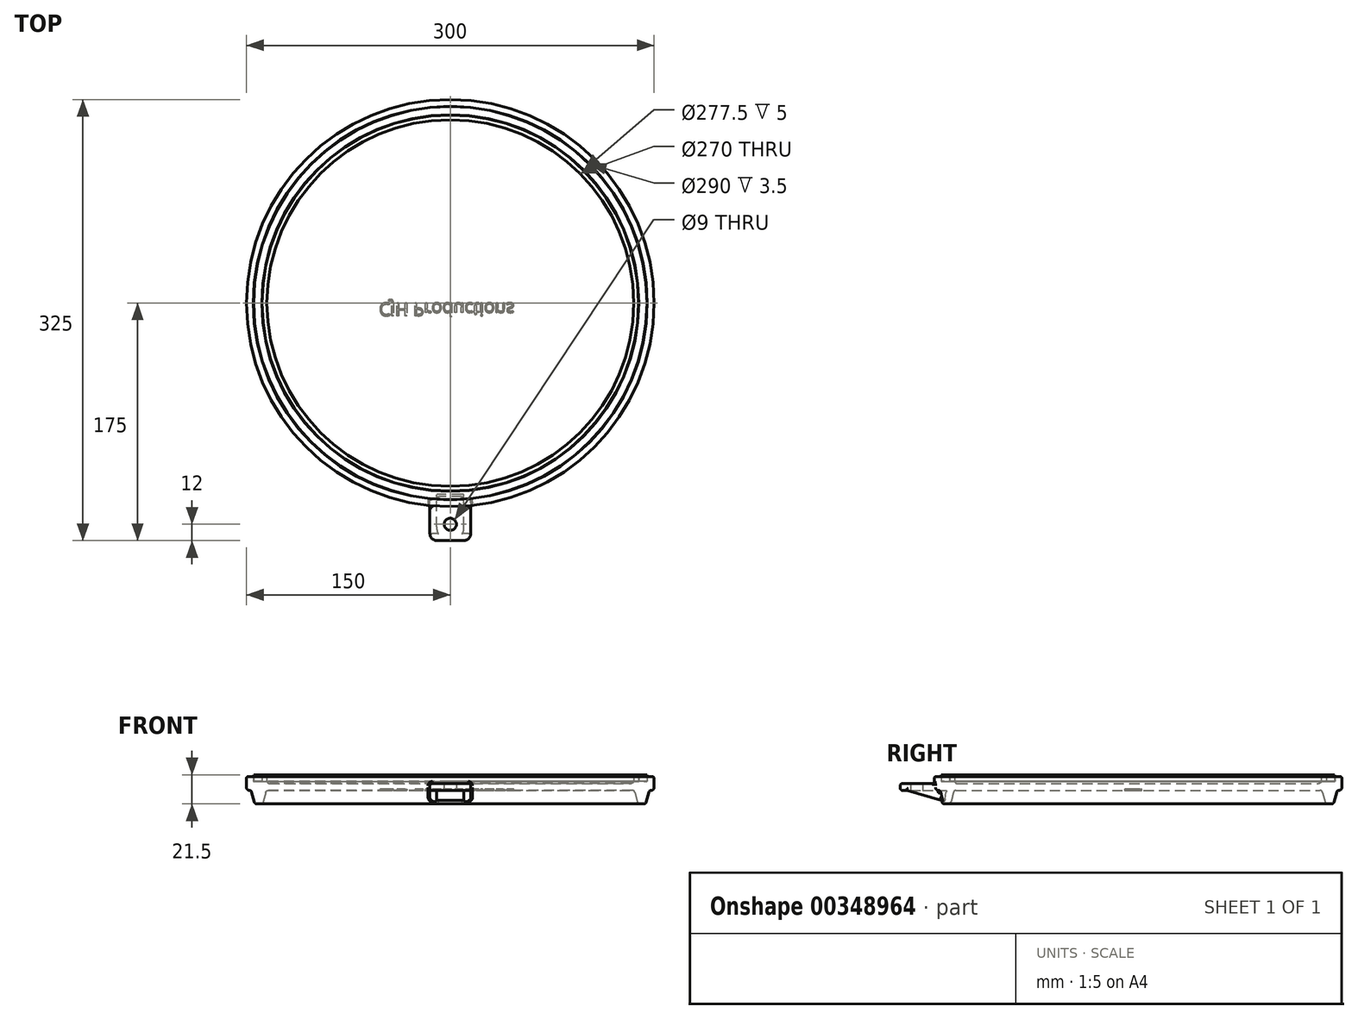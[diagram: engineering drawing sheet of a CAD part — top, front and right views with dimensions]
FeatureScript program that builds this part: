
annotation { "Feature Type Name" : "Feature", "Feature Type Description" : "" }
export const myFeature = defineFeature(function(context is Context, id is Id, definition is map)
    precondition{}
    {
        {
            var Q0;
            Q0=qCreatedBy(makeId("Front.planeOp"),FACE);
            var sketch = newSketch(context, id + "F0", { "sketchPlane" : qUnion([Q0])});
            skLineSegment(sketch, "E0", {"start": v(0, 0) * mm, "end": v(-133.94, 0) * mm});
            skLineSegment(sketch, "E1", {"start": v(-150, 2) * mm, "end": v(-150, 9) * mm});
            skLineSegment(sketch, "E2", {"start": v(-149, 10) * mm, "end": v(-145, 10) * mm});
            skLineSegment(sketch, "E3", {"start": v(-145, 10) * mm, "end": v(-145, 6.5) * mm});
            skLineSegment(sketch, "E4", {"start": v(-145, 6.5) * mm, "end": v(-138.5, 6.5) * mm});
            skLineSegment(sketch, "E5", {"start": v(-138.5, 6.5) * mm, "end": v(-138.5, 10) * mm});
            skLineSegment(sketch, "E6", {"start": v(-138.5, 10) * mm, "end": v(-136, 10) * mm});
            skLineSegment(sketch, "E7", {"start": v(-135, 9) * mm, "end": v(-135, 7) * mm});
            skLineSegment(sketch, "E8", {"start": v(-133, 5) * mm, "end": v(0, 5) * mm});
            skLineSegment(sketch, "E9", {"start": v(0, -14.03) * mm, "end": v(0, 19) * mm, "construction": true});
            skLineSegment(sketch, "E10", {"start": v(-146.12, -1.51) * mm, "end": v(-144.38, -8.49) * mm});
            skLineSegment(sketch, "E11", {"start": v(-142.44, -10) * mm, "end": v(-139.56, -10) * mm});
            skLineSegment(sketch, "E12", {"start": v(-137.62, -8.49) * mm, "end": v(-135.88, -1.51) * mm});
            skPoint(sketch, "E13.visualSharp", {"position": v(-150, 0) * mm});
            skArc(sketch, "E13.filletArc", {"start": v(-150, 2) * mm, "mid": v(-149.43, 0.6) * mm, "end": v(-148.03, 0) * mm});
            skArc(sketch, "E14.filletArc", {"start": v(-133.94, 0) * mm, "mid": v(-135.17, -0.42) * mm, "end": v(-135.88, -1.51) * mm});
            skPoint(sketch, "E15.newPointB", {"position": v(-146.5, 0) * mm});
            skArc(sketch, "E15.filletArc", {"start": v(-146.12, -1.51) * mm, "mid": v(-146.82, -0.43) * mm, "end": v(-148.03, 0) * mm});
            skPoint(sketch, "E16.visualSharp", {"position": v(-144, -10) * mm});
            skArc(sketch, "E16.filletArc", {"start": v(-144.38, -8.49) * mm, "mid": v(-143.67, -9.58) * mm, "end": v(-142.44, -10) * mm});
            skPoint(sketch, "E17.visualSharp", {"position": v(-138, -10) * mm});
            skArc(sketch, "E17.filletArc", {"start": v(-139.56, -10) * mm, "mid": v(-138.33, -9.58) * mm, "end": v(-137.62, -8.49) * mm});
            skPoint(sketch, "E18.visualSharp", {"position": v(-135, 5) * mm});
            skArc(sketch, "E18.filletArc", {"start": v(-135, 7) * mm, "mid": v(-134.41, 5.59) * mm, "end": v(-133, 5) * mm});
            skPoint(sketch, "E19.visualSharp", {"position": v(-150, 10) * mm});
            skArc(sketch, "E19.filletArc", {"start": v(-149, 10) * mm, "mid": v(-149.7, 9.7) * mm, "end": v(-150, 9) * mm});
            skPoint(sketch, "E20.visualSharp", {"position": v(-135, 10) * mm});
            skArc(sketch, "E20.filletArc", {"start": v(-135, 9) * mm, "mid": v(-135.3, 9.7) * mm, "end": v(-136, 10) * mm});
            skLineSegment(sketch, "E21", {"start": v(0, 0) * mm, "end": v(0, 5) * mm});
            skSolve(sketch);
        }
        {
            var Q0;
            Q0=makeQuery(id+"F0.imprint","IMPRINT",FACE,{"disambiguationData":[TD([[makeQuery(id+"F0.imprint","IMPRINT",EDGE,{"derivedFrom":sQuery(id+"F0.wireOp",EDGE,"E0")}),-1.0]])]});
            var Q1;
            Q1=sQuery(id+"F0.wireOp",EDGE,"E9");
            revolve(context, id + "F1", {"entities" : qUnion([Q0]), "axis" : qUnion([Q1]), "revolveType" : RevolveType.FULL});
        }
        {
            var Q0;
            Q0=qCreatedBy(makeId("Front.planeOp"),FACE);
            var sketch = newSketch(context, id + "F2", { "sketchPlane" : qUnion([Q0])});
            skLineSegment(sketch, "E22", {"start": v(-144, 5) * mm, "end": v(-175, 5) * mm});
            skLineSegment(sketch, "E23", {"start": v(-175, 5) * mm, "end": v(-175, 0) * mm});
            skLineSegment(sketch, "E24", {"start": v(-175, 0) * mm, "end": v(-141, 0) * mm});
            skLineSegment(sketch, "E25", {"start": v(-170, 0) * mm, "end": v(-142.44, -8) * mm});
            skLineSegment(sketch, "E26", {"start": v(-144, 5) * mm, "end": v(-141, 0) * mm});
            skLineSegment(sketch, "E27", {"start": v(-142.44, -8) * mm, "end": v(-141, 0) * mm});
            skSolve(sketch);
        }
        {
            var Q0;
            Q0=makeQuery(id+"F2.imprint","IMPRINT",FACE,{"disambiguationData":[TD([[makeQuery(id+"F2.imprint","IMPRINT",EDGE,{"derivedFrom":sQuery(id+"F2.wireOp",EDGE,"E22")}),1.0]])]});
            var Q1;
            {var subQ2=sQuery(id+"F2.wireOp",EDGE,"E25");Q1=makeQuery(id+"F2.imprint","IMPRINT",FACE,{"disambiguationData":[TD([[makeQuery(id+"F2.imprint","IMPRINT",EDGE,{"derivedFrom":subQ2}),1.0]])]});}
            extrude(context, id + "F3", {"entities" : qUnion([Q0, Q1]), "depth" : 30 * mm, "symmetric" : true});
        }
        {
            var Q0;
            {var subQ2=sQuery(id+"F2.wireOp",EDGE,"E25");Q0=makeQuery(id+"F2.imprint","IMPRINT",FACE,{"disambiguationData":[TD([[makeQuery(id+"F2.imprint","IMPRINT",EDGE,{"derivedFrom":subQ2}),1.0]])]});}
            var Q1;
            {var subQ0=sQuery(id+"F2.wireOp",EDGE,"E22");var subQ1=sQuery(id+"F2.wireOp",EDGE,"E23");var subQ2=sQuery(id+"F2.wireOp",EDGE,"E24");Q1=makeQuery(id+"F3.boolean.opBoolean","SPLIT",FACE,{"disambiguationData":[TD([makeQuery(id+"F1.opRevolve","SWEPT_FACE",FACE,{"disambiguationData":[OSD([sQuery(id+"F0.wireOp",EDGE,"E1")])]})])],"derivedFrom":makeQuery(id+"F3.opExtrude","CAP_FACE",FACE,{"disambiguationData":[OSD([subQ0,subQ1,subQ2,sQuery(id+"F2.wireOp",EDGE,"E26")])],"isStart":false})});}
            var Q2;
            {var subQ0=sQuery(id+"F2.wireOp",EDGE,"E22");var subQ1=sQuery(id+"F2.wireOp",EDGE,"E23");var subQ2=sQuery(id+"F2.wireOp",EDGE,"E24");Q2=makeQuery(id+"F3.boolean.opBoolean","SPLIT",FACE,{"disambiguationData":[TD([makeQuery(id+"F1.opRevolve","SWEPT_FACE",FACE,{"disambiguationData":[OSD([sQuery(id+"F0.wireOp",EDGE,"E1")])]})])],"derivedFrom":makeQuery(id+"F3.opExtrude","CAP_FACE",FACE,{"disambiguationData":[OSD([subQ0,subQ1,subQ2,sQuery(id+"F2.wireOp",EDGE,"E26")])],"isStart":true})});}
            extrude(context, id + "F4", {"entities" : qUnion([Q0]), "operationType" : NewBodyOperationType.REMOVE, "endBoundEntityFace" : qUnion([Q1]), "depth" : 20 * mm, "hasSecondDirection" : true, "secondDirectionBound" : BoundingType.UP_TO_SURFACE, "secondDirectionOppositeDirection" : true, "secondDirectionBoundEntityFace" : qUnion([Q2]), "secondDirectionDepth" : 25 * mm, "symmetric" : true});
        }
        {
            var Q0;
            Q0=makeQuery(id+"F1.opRevolve","SWEPT_BODY",BODY,{"disambiguationData":[OSD([sQuery(id+"F0.wireOp",EDGE,"E0"),sQuery(id+"F0.wireOp",EDGE,"E1"),sQuery(id+"F0.wireOp",EDGE,"E2"),sQuery(id+"F0.wireOp",EDGE,"E3"),sQuery(id+"F0.wireOp",EDGE,"E4"),sQuery(id+"F0.wireOp",EDGE,"E5"),sQuery(id+"F0.wireOp",EDGE,"E6"),sQuery(id+"F0.wireOp",EDGE,"E7"),sQuery(id+"F0.wireOp",EDGE,"E8"),sQuery(id+"F0.wireOp",EDGE,"E10"),sQuery(id+"F0.wireOp",EDGE,"E11"),sQuery(id+"F0.wireOp",EDGE,"E12"),sQuery(id+"F0.wireOp",EDGE,"E13.filletArc"),sQuery(id+"F0.wireOp",EDGE,"E14.filletArc"),sQuery(id+"F0.wireOp",EDGE,"E15.filletArc"),sQuery(id+"F0.wireOp",EDGE,"E16.filletArc"),sQuery(id+"F0.wireOp",EDGE,"E17.filletArc"),sQuery(id+"F0.wireOp",EDGE,"E18.filletArc"),sQuery(id+"F0.wireOp",EDGE,"E19.filletArc"),sQuery(id+"F0.wireOp",EDGE,"E20.filletArc"),sQuery(id+"F0.wireOp",EDGE,"E21")])]});
            var Q1;
            Q1=makeQuery(id+"F3.opExtrude","SWEPT_BODY",BODY,{"disambiguationData":[OSD([sQuery(id+"F2.wireOp",EDGE,"E22"),sQuery(id+"F2.wireOp",EDGE,"E23"),sQuery(id+"F2.wireOp",EDGE,"E24"),sQuery(id+"F2.wireOp",EDGE,"E25"),sQuery(id+"F2.wireOp",EDGE,"E26"),sQuery(id+"F2.wireOp",EDGE,"E27")])]});
            booleanBodies(context, id + "F5", {"operationType" : BooleanOperationType.UNION, "tools" : qUnion([Q0, Q1])});
        }
        {
            var Q0;
            {var subQ0=sQuery(id+"F2.wireOp",EDGE,"E23");var subQ4=sQuery(id+"F2.wireOp",EDGE,"E24");Q0=makeQuery(id+"F5.opBoolean","SPLIT",FACE,{"disambiguationData":[TD([makeQuery(id+"F3.opExtrude","SWEPT_FACE",FACE,{"disambiguationData":[OSD([subQ0])]})])],"derivedFrom":makeQuery(id+"F4.boolean.opBoolean","MERGE",FACE,{"derivedFrom":[makeQuery(id+"F3.opExtrude","SWEPT_FACE",FACE,{"disambiguationData":[OSD([subQ4])]}),makeQuery(id+"F4.opExtrude","SWEPT_FACE",FACE,{"disambiguationData":[OSD([subQ4])]})]})});}
            var sketch = newSketch(context, id + "F6", { "sketchPlane" : qUnion([Q0])});
            skCircle(sketch, "E28", {"center": v(-163, 0) * mm, "radius": 4.5 * mm});
            skSolve(sketch);
        }
        {
            var Q0;
            Q0=makeQuery(id+"F6.imprint","IMPRINT",FACE,{"disambiguationData":[TD([[makeQuery(id+"F6.imprint","IMPRINT",EDGE,{"derivedFrom":sQuery(id+"F6.wireOp",EDGE,"E28")}),1.0]])]});
            extrude(context, id + "F7", {"entities" : qUnion([Q0]), "operationType" : NewBodyOperationType.REMOVE, "endBound" : BoundingType.THROUGH_ALL, "oppositeDirection" : true, "depth" : 25 * mm});
        }
        {
            var Q0;
            Q0=makeQuery(id+"F3.opExtrude","CAP_EDGE",EDGE,{"disambiguationData":[OSD([sQuery(id+"F2.wireOp",EDGE,"E23")])],"isStart":false});
            var Q1;
            Q1=makeQuery(id+"F3.opExtrude","CAP_EDGE",EDGE,{"disambiguationData":[OSD([sQuery(id+"F2.wireOp",EDGE,"E23")])],"isStart":true});
            fillet(context, id + "F8", {"entities" : qUnion([Q0, Q1]), "radius" : 5 * mm, "tangentPropagation" : true, "allowEdgeOverflow" : false});
        }
        {
            var Q0;
            Q0=makeQuery(id+"F3.opExtrude","SWEPT_EDGE",EDGE,{"disambiguationData":[OSD([sQuery(id+"F2.wireOp",EDGE,"E23"),sQuery(id+"F2.wireOp",EDGE,"E24")])]});
            var Q1;
            {var subQ0=sQuery(id+"F2.wireOp",EDGE,"E23");var subQ4=sQuery(id+"F2.wireOp",EDGE,"E24");Q1=makeQuery(id+"F8.opFillet","BLEND_EDGE",EDGE,{"blendedFrom":[makeQuery(id+"F3.opExtrude","CAP_EDGE",EDGE,{"disambiguationData":[OSD([subQ0])],"isStart":true}),makeQuery(id+"F5.opBoolean","SPLIT",FACE,{"disambiguationData":[TD([makeQuery(id+"F3.opExtrude","SWEPT_FACE",FACE,{"disambiguationData":[OSD([subQ0])]})])],"derivedFrom":makeQuery(id+"F4.boolean.opBoolean","MERGE",FACE,{"derivedFrom":[makeQuery(id+"F3.opExtrude","SWEPT_FACE",FACE,{"disambiguationData":[OSD([subQ4])]}),makeQuery(id+"F4.opExtrude","SWEPT_FACE",FACE,{"disambiguationData":[OSD([subQ4])]})]})})],"blendedInto":[makeQuery(id+"F5.opBoolean","SPLIT",FACE,{"disambiguationData":[TD([makeQuery(id+"F3.opExtrude","SWEPT_FACE",FACE,{"disambiguationData":[OSD([subQ0])]})])],"derivedFrom":makeQuery(id+"F4.boolean.opBoolean","MERGE",FACE,{"derivedFrom":[makeQuery(id+"F3.opExtrude","SWEPT_FACE",FACE,{"disambiguationData":[OSD([subQ4])]}),makeQuery(id+"F4.opExtrude","SWEPT_FACE",FACE,{"disambiguationData":[OSD([subQ4])]})]})})]});}
            var Q2;
            Q2=makeQuery(id+"F3.opExtrude","CAP_EDGE",EDGE,{"disambiguationData":[OSD([sQuery(id+"F2.wireOp",EDGE,"E25")])],"isStart":true});
            var Q3;
            Q3=makeQuery(id+"F3.opExtrude","CAP_EDGE",EDGE,{"disambiguationData":[OSD([sQuery(id+"F2.wireOp",EDGE,"E25")])],"isStart":false});
            var Q4;
            Q4=makeQuery(id+"F4.boolean.opBoolean","COPY",EDGE,{"derivedFrom":makeQuery(id+"F4.opExtrude","CAP_EDGE",EDGE,{"disambiguationData":[OSD([sQuery(id+"F2.wireOp",EDGE,"E25")])],"isStart":true})});
            var Q5;
            Q5=makeQuery(id+"F4.boolean.opBoolean","COPY",EDGE,{"derivedFrom":makeQuery(id+"F4.opExtrude","CAP_EDGE",EDGE,{"disambiguationData":[OSD([sQuery(id+"F2.wireOp",EDGE,"E25")])],"isStart":false})});
            var Q6;
            Q6=makeQuery(id+"F3.opExtrude","SWEPT_EDGE",EDGE,{"disambiguationData":[OSD([sQuery(id+"F2.wireOp",EDGE,"E22"),sQuery(id+"F2.wireOp",EDGE,"E23")])]});
            var Q7;
            {var subQ0=sQuery(id+"F2.wireOp",EDGE,"E24");var subQ1=sQuery(id+"F2.wireOp",EDGE,"E25");Q7=makeQuery(id+"F5.opBoolean","SPLIT",EDGE,{"disambiguationData":[TD([makeQuery(id+"F3.opExtrude","SWEPT_FACE",FACE,{"disambiguationData":[OSD([subQ1])]})])],"derivedFrom":makeQuery(id+"F4.boolean.opBoolean","COPY",EDGE,{"derivedFrom":makeQuery(id+"F4.opExtrude","CAP_EDGE",EDGE,{"disambiguationData":[OSD([subQ0])],"isStart":false})})});}
            var Q8;
            {var subQ0=sQuery(id+"F2.wireOp",EDGE,"E24");var subQ1=sQuery(id+"F2.wireOp",EDGE,"E25");Q8=makeQuery(id+"F5.opBoolean","SPLIT",EDGE,{"disambiguationData":[TD([makeQuery(id+"F3.opExtrude","SWEPT_FACE",FACE,{"disambiguationData":[OSD([subQ1])]})])],"derivedFrom":makeQuery(id+"F4.boolean.opBoolean","COPY",EDGE,{"derivedFrom":makeQuery(id+"F4.opExtrude","CAP_EDGE",EDGE,{"disambiguationData":[OSD([subQ0])],"isStart":true})})});}
            fillet(context, id + "F9", {"entities" : qUnion([Q0, Q1, Q2, Q3, Q4, Q5, Q6, Q7, Q8]), "radius" : 1.5 * mm, "tangentPropagation" : true, "allowEdgeOverflow" : false});
        }
        {
            var Q0;
            Q0=makeQuery(id+"F5.opBoolean","INTERSECT",EDGE,{"derivedFrom":[makeQuery(id+"F1.opRevolve","SWEPT_FACE",FACE,{"disambiguationData":[OSD([sQuery(id+"F0.wireOp",EDGE,"E1")])]}),makeQuery(id+"F3.opExtrude","SWEPT_FACE",FACE,{"disambiguationData":[OSD([sQuery(id+"F2.wireOp",EDGE,"E22")])]})]});
            fillet(context, id + "F10", {"entities" : qUnion([Q0]), "radius" : 1.5 * mm, "tangentPropagation" : true, "allowEdgeOverflow" : false});
        }
        {
            var Q0;
            Q0=makeQuery(id+"F1.opRevolve","SWEPT_BODY",BODY,{"disambiguationData":[OSD([sQuery(id+"F0.wireOp",EDGE,"E0"),sQuery(id+"F0.wireOp",EDGE,"E1"),sQuery(id+"F0.wireOp",EDGE,"E2"),sQuery(id+"F0.wireOp",EDGE,"E3"),sQuery(id+"F0.wireOp",EDGE,"E4"),sQuery(id+"F0.wireOp",EDGE,"E5"),sQuery(id+"F0.wireOp",EDGE,"E6"),sQuery(id+"F0.wireOp",EDGE,"E7"),sQuery(id+"F0.wireOp",EDGE,"E8"),sQuery(id+"F0.wireOp",EDGE,"E10"),sQuery(id+"F0.wireOp",EDGE,"E11"),sQuery(id+"F0.wireOp",EDGE,"E12"),sQuery(id+"F0.wireOp",EDGE,"E13.filletArc"),sQuery(id+"F0.wireOp",EDGE,"E14.filletArc"),sQuery(id+"F0.wireOp",EDGE,"E15.filletArc"),sQuery(id+"F0.wireOp",EDGE,"E16.filletArc"),sQuery(id+"F0.wireOp",EDGE,"E17.filletArc"),sQuery(id+"F0.wireOp",EDGE,"E18.filletArc"),sQuery(id+"F0.wireOp",EDGE,"E19.filletArc"),sQuery(id+"F0.wireOp",EDGE,"E20.filletArc"),sQuery(id+"F0.wireOp",EDGE,"E21")])]});
            var Q1;
            Q1=sQuery(id+"F0.wireOp",EDGE,"E9");
            transform(context, id + "F11", {"entities" : qUnion([Q0]), "transformType" : TransformType.ROTATION, "transformAxis" : qUnion([Q1]), "angle" : 90 * degree, "makeCopy" : false});
        }
        {
            var Q0;
            Q0=makeQuery(id+"F1.opRevolve","SWEPT_FACE",FACE,{"disambiguationData":[OSD([sQuery(id+"F0.wireOp",EDGE,"E0")])]});
            var sketch = newSketch(context, id + "F12", { "sketchPlane" : qUnion([Q0])});
            skText(sketch, "E29", { "text": "CJH Productions", "fontName": "OpenSans-Regular.ttf"});
            const initialGuessF12  = {"E29": [-0.0525, -0.00014, 1, 0, 0.00956]};
            skSetInitialGuess(sketch, initialGuessF12);
            skSolve(sketch);
        }
        {
            var Q0;
            Q0 = qSketchRegion(id + "F12", true);
            extrude(context, id + "F13", {"entities" : qUnion([Q0]), "operationType" : NewBodyOperationType.REMOVE, "oppositeDirection" : true, "depth" : 1 * mm, "hasDraft" : true, "draftAngle" : 3 * degree});
        }
        {
            var Q0;
            Q0=qCreatedBy(makeId("Front.planeOp"),FACE);
            var sketch = newSketch(context, id + "F14", { "sketchPlane" : qUnion([Q0])});
            skLineSegment(sketch, "E30.0", {"start": v(-145, 6.5) * mm, "end": v(-138.5, 6.5) * mm, "construction": true});
            skLineSegment(sketch, "E30.1", {"start": v(0, -14.03) * mm, "end": v(0, 19) * mm, "construction": true});
            skLineSegment(sketch, "E31.bottom", {"start": v(-138.75, 6.5) * mm, "end": v(-144.75, 6.5) * mm});
            skLineSegment(sketch, "E31.top", {"start": v(-138.75, 11.5) * mm, "end": v(-144.75, 11.5) * mm});
            skLineSegment(sketch, "E31.left", {"start": v(-138.75, 6.5) * mm, "end": v(-138.75, 11.5) * mm});
            skLineSegment(sketch, "E31.right", {"start": v(-144.75, 6.5) * mm, "end": v(-144.75, 11.5) * mm});
            skPoint(sketch, "E31.middle", {"position": v(-141.75, 9) * mm});
            skPoint(sketch, "E31.middle.positionSnap0", {"position": v(-141.75, 6.5) * mm});
            skPoint(sketch, "E31.centerSnap0", {"position": v(-141.75, 6.5) * mm});
            skSolve(sketch);
        }
        {
            var Q0;
            Q0=makeQuery(id+"F14.imprint","IMPRINT",FACE,{"disambiguationData":[TD([[makeQuery(id+"F14.imprint","IMPRINT",EDGE,{"derivedFrom":sQuery(id+"F14.wireOp",EDGE,"E31.bottom")}),-1.0]])]});
            var Q1;
            Q1=sQuery(id+"F14.wireOp",EDGE,"E30.1");
            revolve(context, id + "F15", {"entities" : qUnion([Q0]), "axis" : qUnion([Q1]), "revolveType" : RevolveType.FULL});
        }
    });
